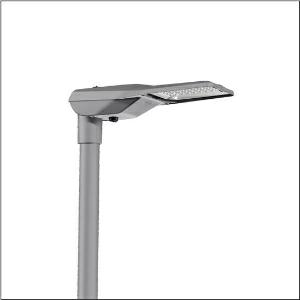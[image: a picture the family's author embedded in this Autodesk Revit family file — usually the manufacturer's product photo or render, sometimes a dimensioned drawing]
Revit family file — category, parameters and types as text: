
# Revit family: streetlight_sl_21_iq_mini___st1_0ab_5xe2m31y08hb_576a
name_source: partatom
category: Lighting Fixtures
units: mm (PartAtom-declared; Revit-internal decimal feet)

## family parameters
Cut with Voids When Loaded = No
Host = Face
Light Source = No
Part Type = Normal
Room Calculation Point = No
Round Connector Dimension = Use Diameter
Shared = No

## types (1)
- --- (1 x LED, 8580 lm, 71 W, 3000K)
    Apparent Load = 71 VA
    CIE Flux Codes = 38 73 97 100 100
    Color Rendering = 70
    Color Temperature = 3000K
    Default Elevation = 1800 mm
    Description = Streetlight SL 21 iQ mini, mast luminaire, primary light control with lens, of PMMA, primary optical cover: cover, of toughened safety glass, transparent, light distribution: ST1.0aB, light emission: direct distribution, primary light characteristic: asymmetric, installation type: post-top, side-entry, LED, High Power LED, rated luminous flux: 8.580lm, luminous efficacy: 121lm/W, light colour: 730, colour temperature: 3000K, control: presetting dimming logarithmic, Street-Remote, Auto-Match, Temp-Guard, Lumen-Switch, Night-Set, Smart-Wire, Light-Fading, Desk-Remote (wireless, voltage-free reading and setting of iQ features in the workshop via application-optimized NFC function/RFID function), optimised constant luminous flux control (CLO 2.0), mains connection: 220..240V, AC, 50/60Hz, start of lifetime: 71W, end of service life: 75W, reduction: 30W, luminaire housing, of diecast aluminium, powder-coated, Siteco® metallic grey (DB 702S), corrosivity category C5 mid according to DIN EN ISO 12944, please order mast flange separately, inclination adjustable: 0°, 5°, 10°, 15°, sealing non-destructively replaceable, multi-level sealing system, length: 628mm, width: 235mm, height: 110mm, mast flange for spigot size: 42mm (side-entry): 5XC10008XM4, 60/48mm (side-entry/post-top): 5XC10108XM2, 76/60mm (side-entry/post-top): 5XC10108XM1, Smart Interface below and above, protection rating (complete): IP66, insulation class (complete): insulation class II (safety insulation), certification: CE, ENEC, ENEC+, VDE, impact resistance: IK09, permissible operating ambient temperature for outdoor applications: -40..+50°C, standard-compliant lighting for roads and squares, packaging unit: 1 piece

Light Distribution: ST1.0aB
    Height = 110 mm
    Lamp = 1 x LED
    Lamp Light Flux = 8580 lm
    Lamp Power = 71 W
    Lamp count = 1
    Length = 625 mm
    Luminous efficacy = 121 lm/W
    Manufacturer = Siteco
    ModVariant = No
    Model = 5XE2M31Y08HB
    Number of Poles = 1
    OnlyDefault = Yes
    Power Factor = 1
    Product Name = Streetlight SL 21 iQ mini | ST1.0aB
    Product group = mast luminaire | pylon top
    ProductGroupID = 6100
    Protection Class = Protection class II
    Protection Degree = IP 66
    RLX_Detail_Level = 1
    RLX_Emergency_Light_Flux = 0 lm
    RLX_Emergency_Type = 0
    RLX_Emergency_Type_DB = No
    RlxData = <blob elided: 92613 chars, md5=08a7e145>
    Socket = socket
    Standby Power = 0 W
    System Light Flux = 8580 lm
    System Power = 71 W
    Type Comments = factory setting: luminous flux: 100 % | dim-lin: 254 | 716 mA
    Type Image = l_1003514.jpg
    URL = http://relux.com
    VarID = @adj_060641
    Voltage = 0 V
    Weight = 0.00 kg
    Width = 234 mm

## geometry (parser evidence)
native form markers: Blend x4, Sweep x12
no freeform markers — native parametric forms only
